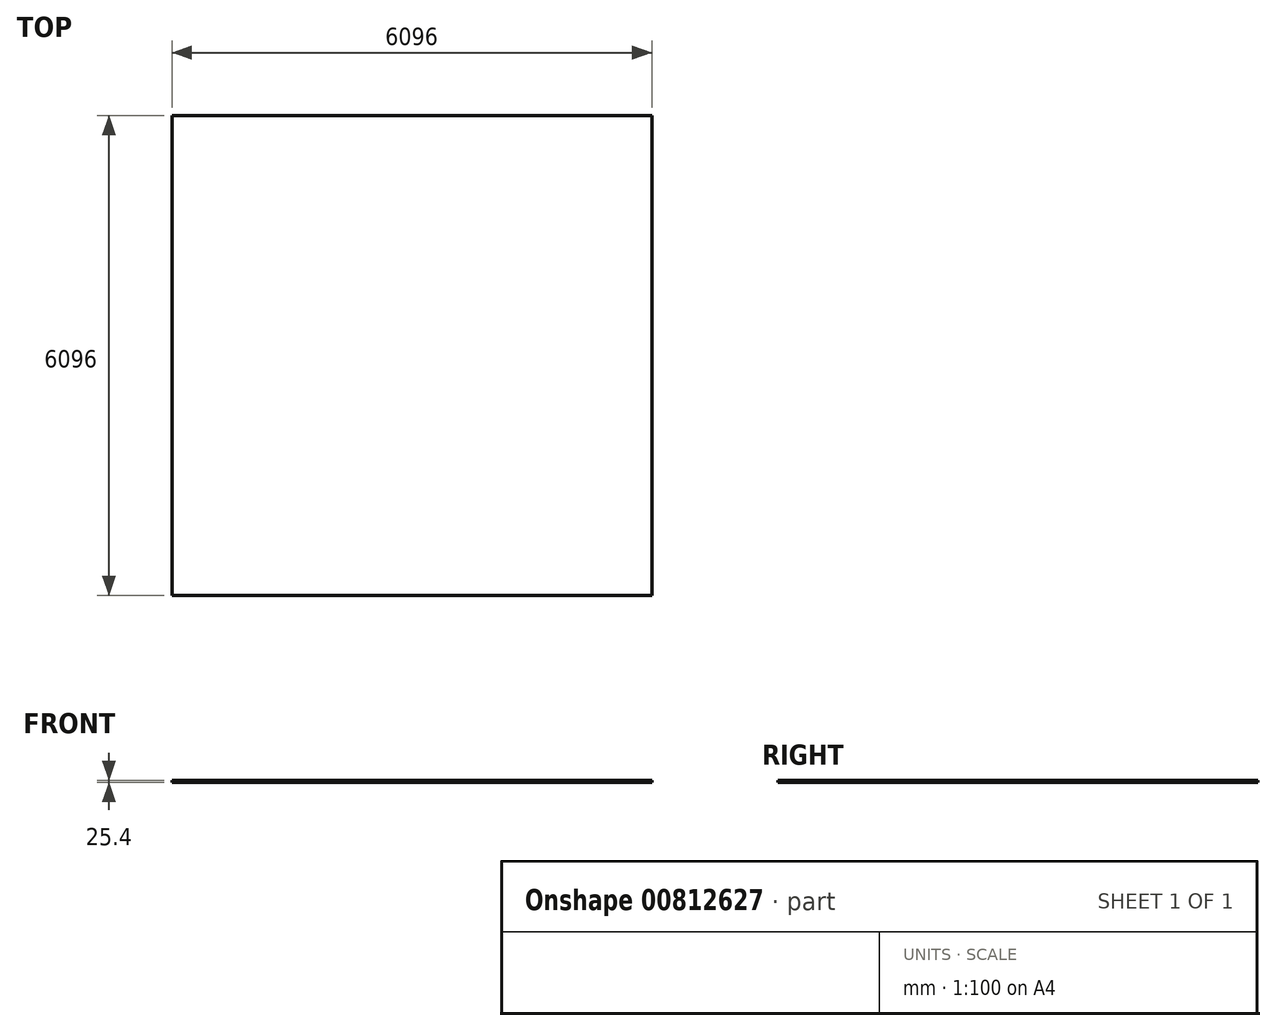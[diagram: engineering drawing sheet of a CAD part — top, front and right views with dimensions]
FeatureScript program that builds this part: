
annotation { "Feature Type Name" : "Feature", "Feature Type Description" : "" }
export const myFeature = defineFeature(function(context is Context, id is Id, definition is map)
    precondition{}
    {
        {
            var Q0;
            Q0=qCreatedBy(makeId("Top.planeOp"),FACE);
            var sketch = newSketch(context, id + "F0", { "sketchPlane" : qUnion([Q0])});
            skLineSegment(sketch, "E0.bottom", {"start": v(3048, 3048) * mm, "end": v(-3048, 3048) * mm});
            skLineSegment(sketch, "E0.top", {"start": v(3048, -3048) * mm, "end": v(-3048, -3048) * mm});
            skLineSegment(sketch, "E0.left", {"start": v(3048, 3048) * mm, "end": v(3048, -3048) * mm});
            skLineSegment(sketch, "E0.right", {"start": v(-3048, 3048) * mm, "end": v(-3048, -3048) * mm});
            skPoint(sketch, "E0.middle", {"position": v(0, 0) * mm});
            skSolve(sketch);
        }
        {
            var Q0;
            Q0 = qSketchRegion(id + "F0", true);
            extrude(context, id + "F1", {"entities" : qUnion([Q0]), "depth" : 25.4 * mm, "offsetDistance" : 25.4 * mm});
        }
    });
